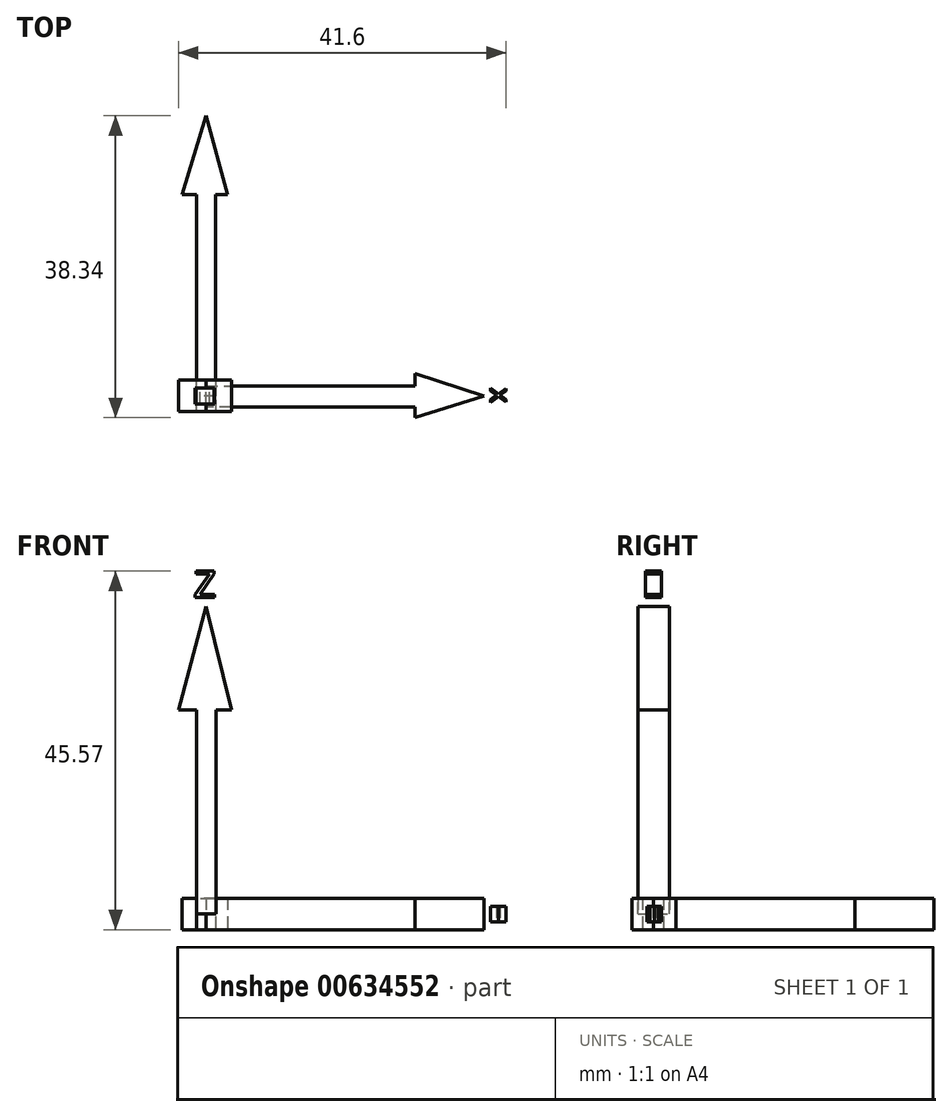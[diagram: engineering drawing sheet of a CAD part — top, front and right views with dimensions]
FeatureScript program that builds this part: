
annotation { "Feature Type Name" : "Feature", "Feature Type Description" : "" }
export const myFeature = defineFeature(function(context is Context, id is Id, definition is map)
    precondition{}
    {
        {
            var Q0;
            Q0=qCreatedBy(makeId("Top.planeOp"),FACE);
            var sketch = newSketch(context, id + "F0", { "sketchPlane" : qUnion([Q0])});
            skLineSegment(sketch, "E0", {"start": v(-1.17, 0) * mm, "end": v(-1.17, 25.6) * mm});
            skLineSegment(sketch, "E1", {"start": v(-1.13, 25.6) * mm, "end": v(-3, 25.6) * mm});
            skLineSegment(sketch, "E2", {"start": v(-3, 25.6) * mm, "end": v(0, 35.6) * mm});
            skLineSegment(sketch, "E3", {"start": v(0, 35.6) * mm, "end": v(2.78, 25.6) * mm});
            skPoint(sketch, "E3.endSnap0", {"position": v(-2.07, 25.6) * mm});
            skLineSegment(sketch, "E4", {"start": v(2.78, 25.6) * mm, "end": v(1.24, 25.6) * mm});
            skLineSegment(sketch, "E5", {"start": v(1.24, 25.6) * mm, "end": v(1.24, 0) * mm});
            skLineSegment(sketch, "E6", {"start": v(1.24, 0) * mm, "end": v(-1.25, 0) * mm});
            skSolve(sketch);
        }
        {
            var Q0;
            Q0=qCreatedBy(makeId("Top.planeOp"),FACE);
            var sketch = newSketch(context, id + "F1", { "sketchPlane" : qUnion([Q0])});
            skLineSegment(sketch, "E7", {"start": v(0, 0) * mm, "end": v(0, 1.28) * mm});
            skLineSegment(sketch, "E8", {"start": v(0, 1.28) * mm, "end": v(26.57, 1.28) * mm});
            skLineSegment(sketch, "E9", {"start": v(26.57, 1.28) * mm, "end": v(26.57, 2.84) * mm});
            skLineSegment(sketch, "E10", {"start": v(26.57, 2.84) * mm, "end": v(35.35, 0) * mm});
            skLineSegment(sketch, "E11", {"start": v(35.35, 0) * mm, "end": v(26.57, -2.74) * mm});
            skLineSegment(sketch, "E12", {"start": v(26.57, -2.74) * mm, "end": v(26.57, -1.4) * mm});
            skLineSegment(sketch, "E13", {"start": v(26.57, -1.4) * mm, "end": v(0, -1.4) * mm});
            skLineSegment(sketch, "E14", {"start": v(0, -1.4) * mm, "end": v(0, 0) * mm});
            skSolve(sketch);
        }
        {
            var Q0;
            Q0 = qSketchRegion(id + "F0", true);
            var Q1;
            Q1 = qSketchRegion(id + "F1", true);
            extrude(context, id + "F2", {"entities" : qUnion([Q0, Q1]), "endBound" : BoundingType.SYMMETRIC, "depth" : 4 * mm, "offsetDistance" : 25.4 * mm});
        }
        {
            var Q0;
            Q0=qCreatedBy(makeId("Front.planeOp"),FACE);
            var sketch = newSketch(context, id + "F3", { "sketchPlane" : qUnion([Q0])});
            skLineSegment(sketch, "E15", {"start": v(0, 0) * mm, "end": v(-1.16, 0) * mm});
            skLineSegment(sketch, "E16", {"start": v(-1.16, 0) * mm, "end": v(-1.16, 25.9) * mm});
            skLineSegment(sketch, "E17", {"start": v(-1.16, 25.9) * mm, "end": v(-5.8, 25.9) * mm});
            skLineSegment(sketch, "E18", {"start": v(-3.48, 25.9) * mm, "end": v(0, 39.07) * mm});
            skLineSegment(sketch, "E19", {"start": v(0, 39.07) * mm, "end": v(3.26, 25.9) * mm});
            skLineSegment(sketch, "E20", {"start": v(3.26, 25.9) * mm, "end": v(1.28, 25.9) * mm});
            skLineSegment(sketch, "E21", {"start": v(1.28, 25.9) * mm, "end": v(1.28, 0) * mm});
            skLineSegment(sketch, "E22", {"start": v(1.28, 0) * mm, "end": v(0, 0) * mm});
            skSolve(sketch);
        }
        {
            var Q0;
            Q0 = qSketchRegion(id + "F3", true);
            extrude(context, id + "F4", {"entities" : qUnion([Q0]), "endBound" : BoundingType.SYMMETRIC, "depth" : 4 * mm, "offsetDistance" : 25 * mm});
        }
        {
            var Q0;
            Q0=qCreatedBy(makeId("Front.planeOp"),FACE);
            var sketch = newSketch(context, id + "F5", { "sketchPlane" : qUnion([Q0])});
            skText(sketch, "E23", { "text": "z", "fontName": "OpenSans-Regular.ttf"});
            const initialGuessF5  = {"E23": [-0.00159, 0.04022, 1, 0, 0.00451]};
            skSetInitialGuess(sketch, initialGuessF5);
            skSolve(sketch);
        }
        {
            var Q0;
            Q0 = qSketchRegion(id + "F5", true);
            extrude(context, id + "F6", {"entities" : qUnion([Q0]), "endBound" : BoundingType.SYMMETRIC, "depth" : 2 * mm, "offsetDistance" : 25 * mm});
        }
        {
            var Q0;
            Q0=qCreatedBy(makeId("Top.planeOp"),FACE);
            var sketch = newSketch(context, id + "F7", { "sketchPlane" : qUnion([Q0])});
            skText(sketch, "E24", { "text": "y", "fontName": "OpenSans-Regular.ttf"});
            const initialGuessF7  = {"E24": [-0.00073, 0.03665, 1, 0, 0.00197]};
            skSetInitialGuess(sketch, initialGuessF7);
            skSolve(sketch);
        }
        {
            var Q0;
            Q0 = qConstructionFilter(qBodyType(qCreatedBy(id + "F7" ,EDGE), BodyType.WIRE), ConstructionObject.NO);
            extrude(context, id + "F8", {"bodyType" : ToolBodyType.SURFACE, "surfaceEntities" : qUnion([Q0]), "endBound" : BoundingType.SYMMETRIC, "depth" : 2 * mm, "offsetDistance" : 25 * mm});
        }
        {
            var Q0;
            Q0=qCreatedBy(makeId("Top.planeOp"),FACE);
            var sketch = newSketch(context, id + "F9", { "sketchPlane" : qUnion([Q0])});
            skText(sketch, "E25", { "text": "x", "fontName": "OpenSans-Regular.ttf"});
            const initialGuessF9  = {"E25": [0.03613, 0.00107, 0, -1, 0.00268]};
            skSetInitialGuess(sketch, initialGuessF9);
            skSolve(sketch);
        }
        {
            var Q0;
            Q0 = qSketchRegion(id + "F9", true);
            extrude(context, id + "F10", {"entities" : qUnion([Q0]), "endBound" : BoundingType.SYMMETRIC, "depth" : 2 * mm, "offsetDistance" : 25 * mm});
        }
    });
